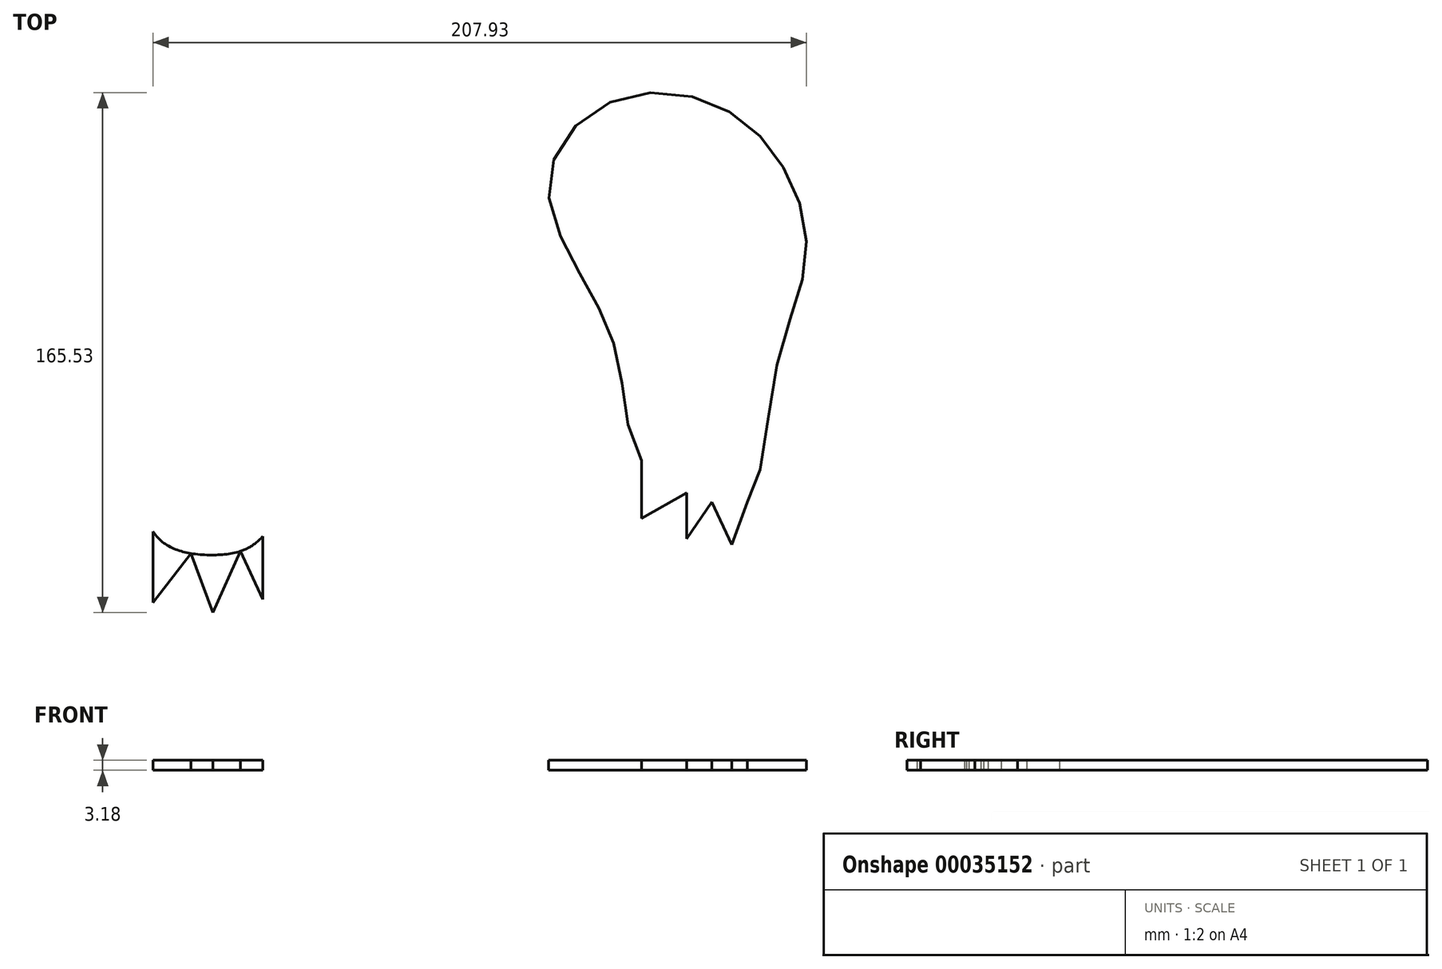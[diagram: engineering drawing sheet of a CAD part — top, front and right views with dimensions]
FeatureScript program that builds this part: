
annotation { "Feature Type Name" : "Feature", "Feature Type Description" : "" }
export const myFeature = defineFeature(function(context is Context, id is Id, definition is map)
    precondition{}
    {
        {
            var Q0;
            Q0=qCreatedBy(makeId("Top.planeOp"),FACE);
            var sketch = newSketch(context, id + "F0", { "sketchPlane" : qUnion([Q0])});
            skFitSpline(sketch, "E0", {"points": [v(77.3, 71.03) * mm, v(99.6, 51.4) * mm, v(107.37, 22.75) * mm, v(97.8, -13.55) * mm, v(88.64, -55.97) * mm, v(77.3, -55.97) * mm, v(54.97, -42.75) * mm, v(47.52, -11.05) * mm, v(35.5, 16.5) * mm, v(25.47, 46.85) * mm, v(44.22, 71.03) * mm, v(77.3, 71.03) * mm]});
            skLineSegment(sketch, "E1", {"start": v(-100.47, -65.38) * mm, "end": v(-100.47, -88) * mm});
            skLineSegment(sketch, "E2", {"start": v(-100.47, -88) * mm, "end": v(-88.45, -72.3) * mm});
            skLineSegment(sketch, "E3", {"start": v(-88.45, -72.3) * mm, "end": v(-81.45, -91.16) * mm});
            skLineSegment(sketch, "E4", {"start": v(-81.45, -91.16) * mm, "end": v(-72.64, -71.59) * mm});
            skLineSegment(sketch, "E5", {"start": v(-72.64, -71.59) * mm, "end": v(-65.58, -86.88) * mm});
            skLineSegment(sketch, "E6", {"start": v(-65.58, -86.88) * mm, "end": v(-65.58, -66.84) * mm});
            skLineSegment(sketch, "E7", {"start": v(54.97, -42.75) * mm, "end": v(54.97, -61.2) * mm});
            skLineSegment(sketch, "E8", {"start": v(54.97, -61.2) * mm, "end": v(69.35, -53.07) * mm});
            skLineSegment(sketch, "E9", {"start": v(69.35, -53.07) * mm, "end": v(69.35, -67.66) * mm});
            skLineSegment(sketch, "E10", {"start": v(69.35, -67.66) * mm, "end": v(77.3, -55.97) * mm});
            skLineSegment(sketch, "E11", {"start": v(77.3, -55.97) * mm, "end": v(83.6, -69.57) * mm});
            skLineSegment(sketch, "E12", {"start": v(83.6, -69.57) * mm, "end": v(88.64, -55.97) * mm});
            skFitSpline(sketch, "E13.trimOffspring", {"points": [v(-81.45, 79.6) * mm, v(-99.12, 79.6) * mm, v(-115.08, 63.36) * mm, v(-125.71, 25.33) * mm, v(-122.98, -8.17) * mm, v(-108.6, -28.2) * mm, v(-100.47, -65.38) * mm, v(-81.45, -72.8) * mm, v(-65.58, -66.84) * mm, v(-51.25, -26.56) * mm, v(-39.22, 21.29) * mm, v(-45.79, 62.92) * mm, v(-81.45, 79.6) * mm]});
            skSolve(sketch);
        }
        {
            var Q0;
            {var subQ1=sQuery(id+"F0.wireOp",EDGE,"115aa28d-62a3-4706-a7cf-55b58465c164");var subQ3=sQuery(id+"F0.wireOp",EDGE,"E0");var subQ5=makeQuery(id+"F0.imprint","INTERSECT",VERTEX,{"derivedFrom":[subQ1,subQ3]});Q0=makeQuery(id+"F0.imprint","IMPRINT",FACE,{"disambiguationData":[TD([[makeQuery(id+"F0.imprint","IMPRINT",EDGE,{"disambiguationData":[TD([[subQ5,-1.0]])],"derivedFrom":subQ1}),1.0]])]});}
            var Q1;
            {var subQ0=sQuery(id+"F0.wireOp",EDGE,"E5");Q1=makeQuery(id+"F0.imprint","IMPRINT",FACE,{"disambiguationData":[TD([[makeQuery(id+"F0.imprint","IMPRINT",EDGE,{"derivedFrom":subQ0}),1.0]])]});}
            var Q2;
            {var subQ1=sQuery(id+"F0.wireOp",EDGE,"8a344740-1494-4c66-a654-d00c580876b4");var subQ3=sQuery(id+"F0.wireOp",EDGE,"a3fdc31a-57c1-4856-b1ae-023aa7ed3109");var subQ7=makeQuery(id+"F0.imprint","INTERSECT",VERTEX,{"disambiguationData":[OD(1.0)],"derivedFrom":[subQ1,subQ3]});Q2=makeQuery(id+"F0.imprint","IMPRINT",FACE,{"disambiguationData":[TD([[makeQuery(id+"F0.imprint","IMPRINT",EDGE,{"disambiguationData":[TD([[subQ7,1.0]])],"derivedFrom":subQ1}),1.0]])]});}
            var Q3;
            {var subQ1=sQuery(id+"F0.wireOp",EDGE,"8a344740-1494-4c66-a654-d00c580876b4");var subQ3=sQuery(id+"F0.wireOp",EDGE,"a3fdc31a-57c1-4856-b1ae-023aa7ed3109");var subQ5=makeQuery(id+"F0.imprint","INTERSECT",VERTEX,{"disambiguationData":[OD(0.0)],"derivedFrom":[subQ1,subQ3]});Q3=makeQuery(id+"F0.imprint","IMPRINT",FACE,{"disambiguationData":[TD([[makeQuery(id+"F0.imprint","IMPRINT",EDGE,{"disambiguationData":[TD([[subQ5,-1.0]])],"derivedFrom":subQ1}),1.0]])]});}
            var Q4;
            {var subQ1=sQuery(id+"F0.wireOp",EDGE,"E9");Q4=makeQuery(id+"F0.imprint","IMPRINT",FACE,{"disambiguationData":[TD([[makeQuery(id+"F0.imprint","IMPRINT",EDGE,{"derivedFrom":subQ1}),1.0]])]});}
            var Q5;
            {var subQ1=sQuery(id+"F0.wireOp",EDGE,"E3");Q5=makeQuery(id+"F0.imprint","IMPRINT",FACE,{"disambiguationData":[TD([[makeQuery(id+"F0.imprint","IMPRINT",EDGE,{"derivedFrom":subQ1}),1.0]])]});}
            var Q6;
            {var subQ1=sQuery(id+"F0.wireOp",EDGE,"8a344740-1494-4c66-a654-d00c580876b4");var subQ3=sQuery(id+"F0.wireOp",EDGE,"a3fdc31a-57c1-4856-b1ae-023aa7ed3109");var subQ5=makeQuery(id+"F0.imprint","INTERSECT",VERTEX,{"disambiguationData":[OD(0.0)],"derivedFrom":[subQ1,subQ3]});Q6=makeQuery(id+"F0.imprint","IMPRINT",FACE,{"disambiguationData":[TD([[makeQuery(id+"F0.imprint","IMPRINT",EDGE,{"disambiguationData":[TD([[subQ5,-1.0]])],"derivedFrom":subQ1}),-1.0]])]});}
            var Q7;
            {var subQ1=sQuery(id+"F0.wireOp",EDGE,"E7");Q7=makeQuery(id+"F0.imprint","IMPRINT",FACE,{"disambiguationData":[TD([[makeQuery(id+"F0.imprint","IMPRINT",EDGE,{"derivedFrom":subQ1}),1.0]])]});}
            var Q8;
            {var subQ1=sQuery(id+"F0.wireOp",EDGE,"E1");Q8=makeQuery(id+"F0.imprint","IMPRINT",FACE,{"disambiguationData":[TD([[makeQuery(id+"F0.imprint","IMPRINT",EDGE,{"derivedFrom":subQ1}),1.0]])]});}
            var Q9;
            {var subQ3=sQuery(id+"F0.wireOp",EDGE,"E0");var subQ5=makeQuery(id+"F0.imprint","INTERSECT",VERTEX,{"derivedFrom":[subQ3,sQuery(id+"F0.wireOp",EDGE,"E7")]});Q9=makeQuery(id+"F0.imprint","IMPRINT",FACE,{"disambiguationData":[TD([[makeQuery(id+"F0.imprint","IMPRINT",EDGE,{"disambiguationData":[TD([[subQ5,-1.0]])],"derivedFrom":subQ3}),-1.0]])]});}
            var Q10;
            {var subQ1=sQuery(id+"F0.wireOp",EDGE,"8a344740-1494-4c66-a654-d00c580876b4");var subQ3=sQuery(id+"F0.wireOp",EDGE,"a3fdc31a-57c1-4856-b1ae-023aa7ed3109");var subQ6=makeQuery(id+"F0.imprint","INTERSECT",VERTEX,{"disambiguationData":[OD(1.0)],"derivedFrom":[subQ1,subQ3]});Q10=makeQuery(id+"F0.imprint","IMPRINT",FACE,{"disambiguationData":[TD([[makeQuery(id+"F0.imprint","IMPRINT",EDGE,{"disambiguationData":[TD([[subQ6,1.0]])],"derivedFrom":subQ1}),-1.0]])]});}
            var Q11;
            {var subQ3=sQuery(id+"F0.wireOp",EDGE,"E0");var subQ5=makeQuery(id+"F0.imprint","INTERSECT",VERTEX,{"derivedFrom":[subQ3,sQuery(id+"F0.wireOp",EDGE,"E12")]});Q11=makeQuery(id+"F0.imprint","IMPRINT",FACE,{"disambiguationData":[TD([[makeQuery(id+"F0.imprint","IMPRINT",EDGE,{"disambiguationData":[TD([[subQ5,1.0]])],"derivedFrom":subQ3}),-1.0]])]});}
            var Q12;
            {var subQ1=sQuery(id+"F0.wireOp",EDGE,"8a344740-1494-4c66-a654-d00c580876b4");var subQ5=sQuery(id+"F0.wireOp",EDGE,"b921b1f0-fb51-44a1-9a93-3b7e9cbc0e22");var subQ6=makeQuery(id+"F0.imprint","INTERSECT",VERTEX,{"derivedFrom":[subQ1,subQ5]});Q12=makeQuery(id+"F0.imprint","IMPRINT",FACE,{"disambiguationData":[TD([[makeQuery(id+"F0.imprint","IMPRINT",EDGE,{"disambiguationData":[TD([[subQ6,-1.0]])],"derivedFrom":subQ1}),1.0]])]});}
            var Q13;
            {var subQ1=sQuery(id+"F0.wireOp",EDGE,"115aa28d-62a3-4706-a7cf-55b58465c164");var subQ3=sQuery(id+"F0.wireOp",EDGE,"E0");var subQ5=makeQuery(id+"F0.imprint","INTERSECT",VERTEX,{"derivedFrom":[subQ1,subQ3]});Q13=makeQuery(id+"F0.imprint","IMPRINT",FACE,{"disambiguationData":[TD([[makeQuery(id+"F0.imprint","IMPRINT",EDGE,{"disambiguationData":[TD([[subQ5,-1.0]])],"derivedFrom":subQ1}),-1.0]])]});}
            var Q14;
            {var subQ1=sQuery(id+"F0.wireOp",EDGE,"E11");Q14=makeQuery(id+"F0.imprint","IMPRINT",FACE,{"disambiguationData":[TD([[makeQuery(id+"F0.imprint","IMPRINT",EDGE,{"derivedFrom":subQ1}),1.0]])]});}
            var Q15;
            {var subQ1=sQuery(id+"F0.wireOp",EDGE,"8a344740-1494-4c66-a654-d00c580876b4");var subQ5=sQuery(id+"F0.wireOp",EDGE,"b921b1f0-fb51-44a1-9a93-3b7e9cbc0e22");var subQ6=makeQuery(id+"F0.imprint","INTERSECT",VERTEX,{"derivedFrom":[subQ1,subQ5]});Q15=makeQuery(id+"F0.imprint","IMPRINT",FACE,{"disambiguationData":[TD([[makeQuery(id+"F0.imprint","IMPRINT",EDGE,{"disambiguationData":[TD([[subQ6,-1.0]])],"derivedFrom":subQ1}),-1.0]])]});}
            extrude(context, id + "F1", {"entities" : qUnion([Q0, Q1, Q2, Q3, Q4, Q5, Q6, Q7, Q8, Q9, Q10, Q11, Q12, Q13, Q14, Q15]), "depth" : 3.17 * mm});
        }
    });
